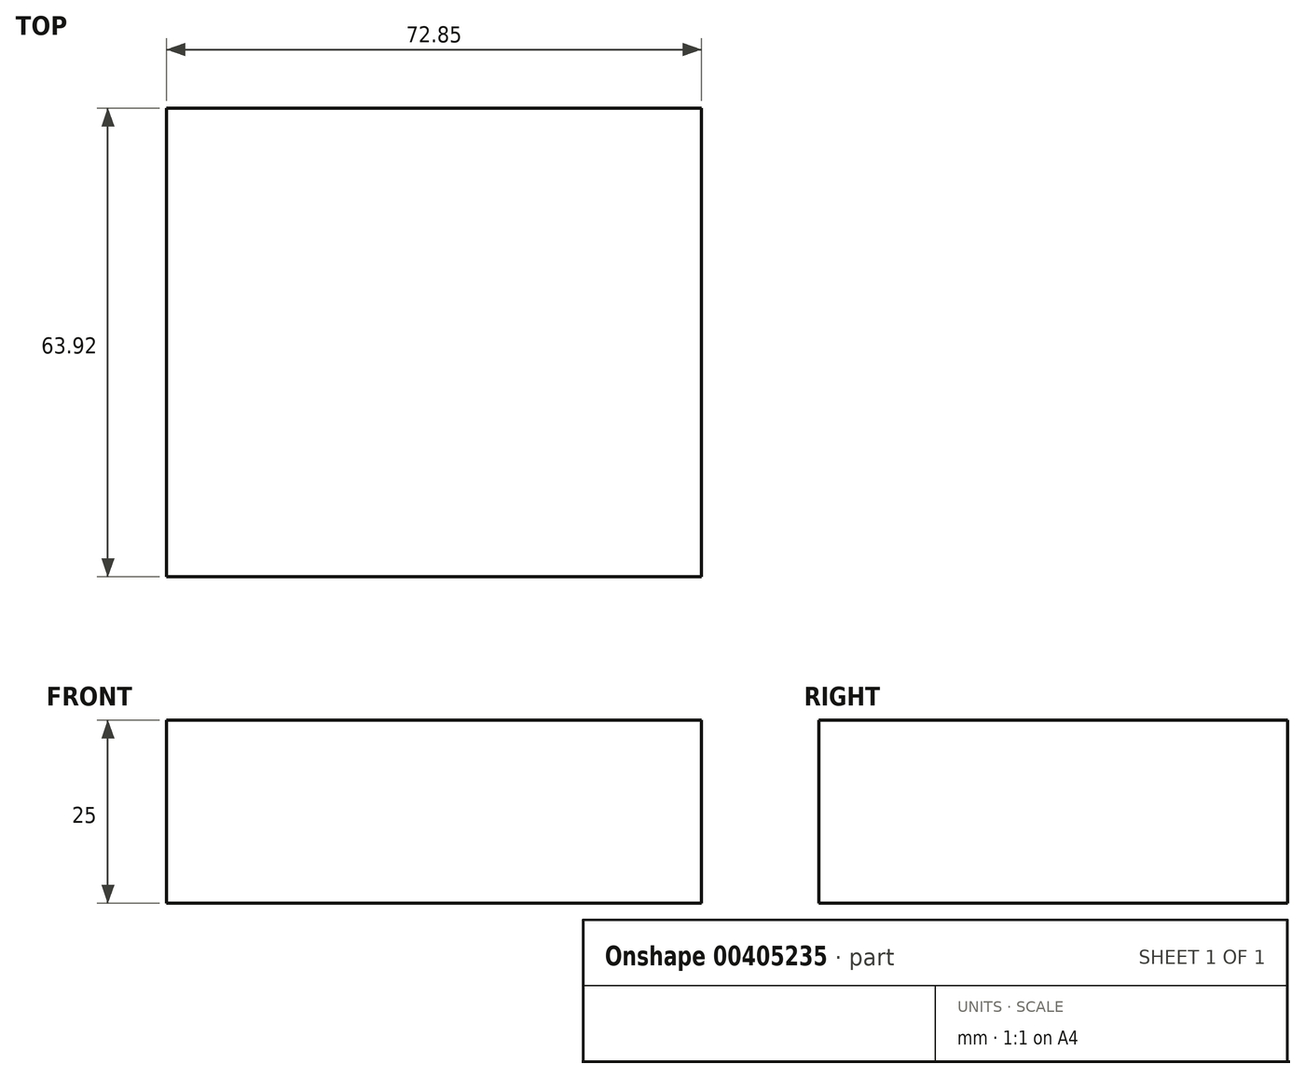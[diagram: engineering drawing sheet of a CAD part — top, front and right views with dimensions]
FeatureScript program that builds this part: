
annotation { "Feature Type Name" : "Feature", "Feature Type Description" : "" }
export const myFeature = defineFeature(function(context is Context, id is Id, definition is map)
    precondition{}
    {
        {
            var Q0;
            Q0=qCreatedBy(makeId("Top.planeOp"),FACE);
            var sketch = newSketch(context, id + "F0", { "sketchPlane" : qUnion([Q0])});
            skLineSegment(sketch, "E0.bottom", {"start": v(-36.93, -33.63) * mm, "end": v(35.92, -33.63) * mm});
            skLineSegment(sketch, "E0.top", {"start": v(-36.93, 30.29) * mm, "end": v(35.92, 30.29) * mm});
            skLineSegment(sketch, "E0.left", {"start": v(-36.93, -33.63) * mm, "end": v(-36.93, 30.29) * mm});
            skLineSegment(sketch, "E0.right", {"start": v(35.92, -33.63) * mm, "end": v(35.92, 30.29) * mm});
            skSolve(sketch);
        }
        {
            var Q0;
            Q0 = qSketchRegion(id + "F0", true);
            extrude(context, id + "F1", {"entities" : qUnion([Q0]), "depth" : 25 * mm});
        }
    });
